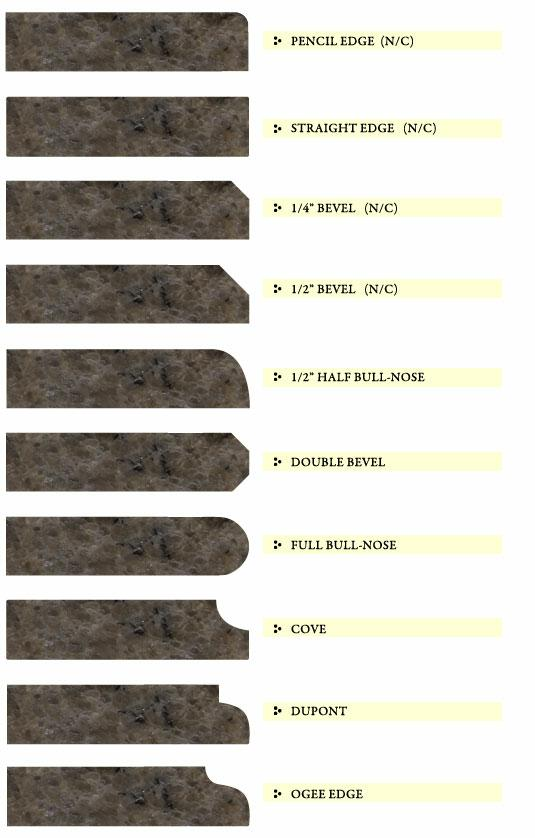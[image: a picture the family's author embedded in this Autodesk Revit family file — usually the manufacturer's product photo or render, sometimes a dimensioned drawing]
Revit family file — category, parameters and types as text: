
# Revit family: Casework-DuPont-Zodiaq-Island-Countertop
name_source: partatom
category: Casework
revit_build: Autodesk Revit Architecture 2015 (Build: 20140903_1530(x64)
units: mm (PartAtom-declared; Revit-internal decimal feet)

## types (2) — shared parameters
1 2 Bevel = No
1 2 Half Bull Nose = No
1 4 Bevel = No
12B = No
12H = No
14B = No
C = No
Cove = No
D = No
DB = No
Description = Quartz Surface Countertop
Double Bevel = No
Dupont = No
FBN = No
Full Bull Nose = No
Height = 3' - 0"
Manufacturer = DuPont
Model = Zodiaq®
OE = No
Ogee Edge = No
PE = No
Pencil Edge = No
Product Name = Zodiaq®
Product Page URL = http://www.dupont.com
SE = Yes
Straight Edge = Yes
zero-valued in all types: Cost

## per-type parameters (varying)
| type | Countertop Material | Depth | Thickness | URL |
| 2cm | Quartz Surface - DuPont - Zodiaq - Névé 2cm | 2' - 0" | 0' - 0 3/4" | http://www.dupont.com |
| 3cm | Quartz Surface - DuPont - Zodiaq - Névé 3cm | 4' - 0" | 0' - 1 3/16" | www.zodiaq.com |

## geometry (parser evidence)
native form markers: Sweep x16
no freeform markers — native parametric forms only
